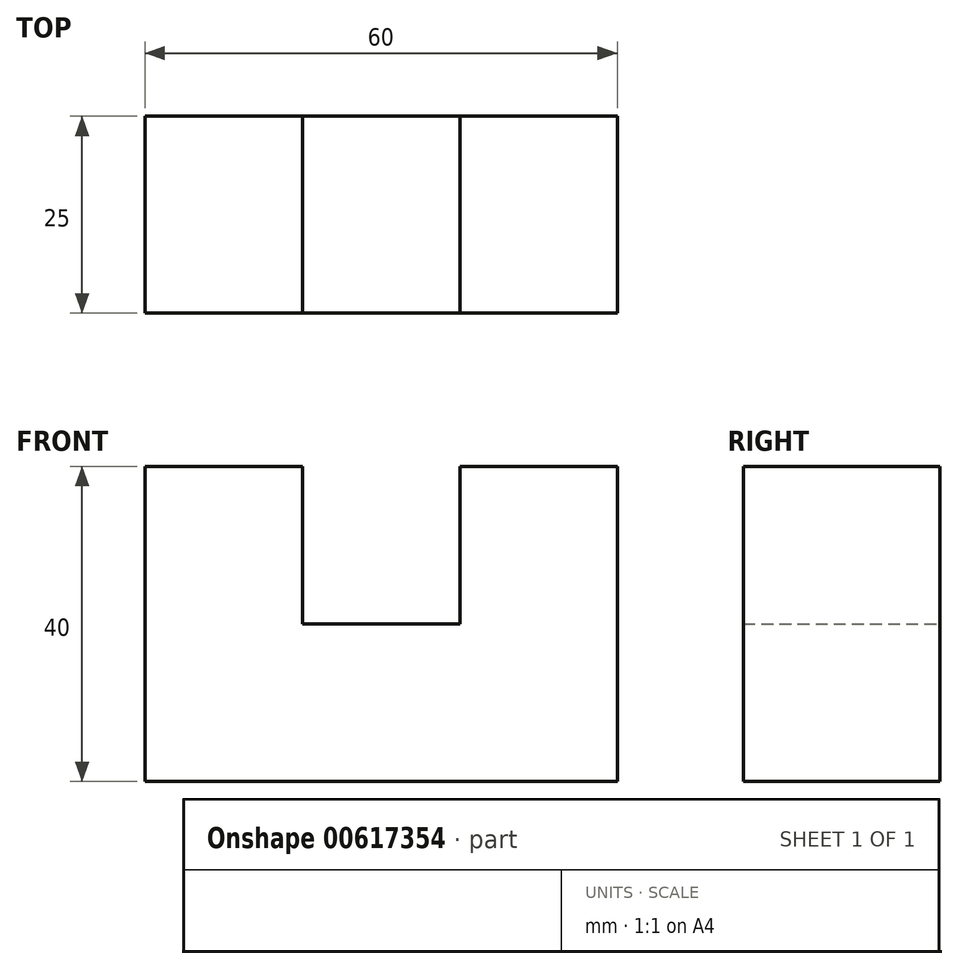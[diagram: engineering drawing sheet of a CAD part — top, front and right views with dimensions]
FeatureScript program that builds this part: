
annotation { "Feature Type Name" : "Feature", "Feature Type Description" : "" }
export const myFeature = defineFeature(function(context is Context, id is Id, definition is map)
    precondition{}
    {
        {
            var Q0;
            Q0=qCreatedBy(makeId("Front.planeOp"),FACE);
            var sketch = newSketch(context, id + "F0", { "sketchPlane" : qUnion([Q0])});
            skLineSegment(sketch, "E0", {"start": v(-33.66, -40) * mm, "end": v(26.34, -40) * mm});
            skLineSegment(sketch, "E1", {"start": v(26.34, -40) * mm, "end": v(26.34, -20) * mm});
            skLineSegment(sketch, "E2", {"start": v(26.34, -20) * mm, "end": v(-33.66, -20) * mm});
            skLineSegment(sketch, "E3", {"start": v(-33.66, -40) * mm, "end": v(-33.66, -20) * mm});
            skLineSegment(sketch, "E4", {"start": v(26.34, -20) * mm, "end": v(26.34, 0) * mm});
            skLineSegment(sketch, "E5", {"start": v(26.34, 0) * mm, "end": v(6.34, 0) * mm});
            skLineSegment(sketch, "E6", {"start": v(6.34, 0) * mm, "end": v(6.34, -20) * mm});
            skLineSegment(sketch, "E7", {"start": v(-33.66, -20) * mm, "end": v(-33.66, 0) * mm});
            skLineSegment(sketch, "E8", {"start": v(-33.66, 0) * mm, "end": v(-13.66, 0) * mm});
            skLineSegment(sketch, "E9", {"start": v(-13.66, 0) * mm, "end": v(-13.66, -20) * mm});
            skSolve(sketch);
        }
        {
            var Q0;
            Q0 = qSketchRegion(id + "F0", true);
            extrude(context, id + "F1", {"entities" : qUnion([Q0]), "depth" : 25 * mm, "offsetDistance" : 25 * mm});
        }
    });
